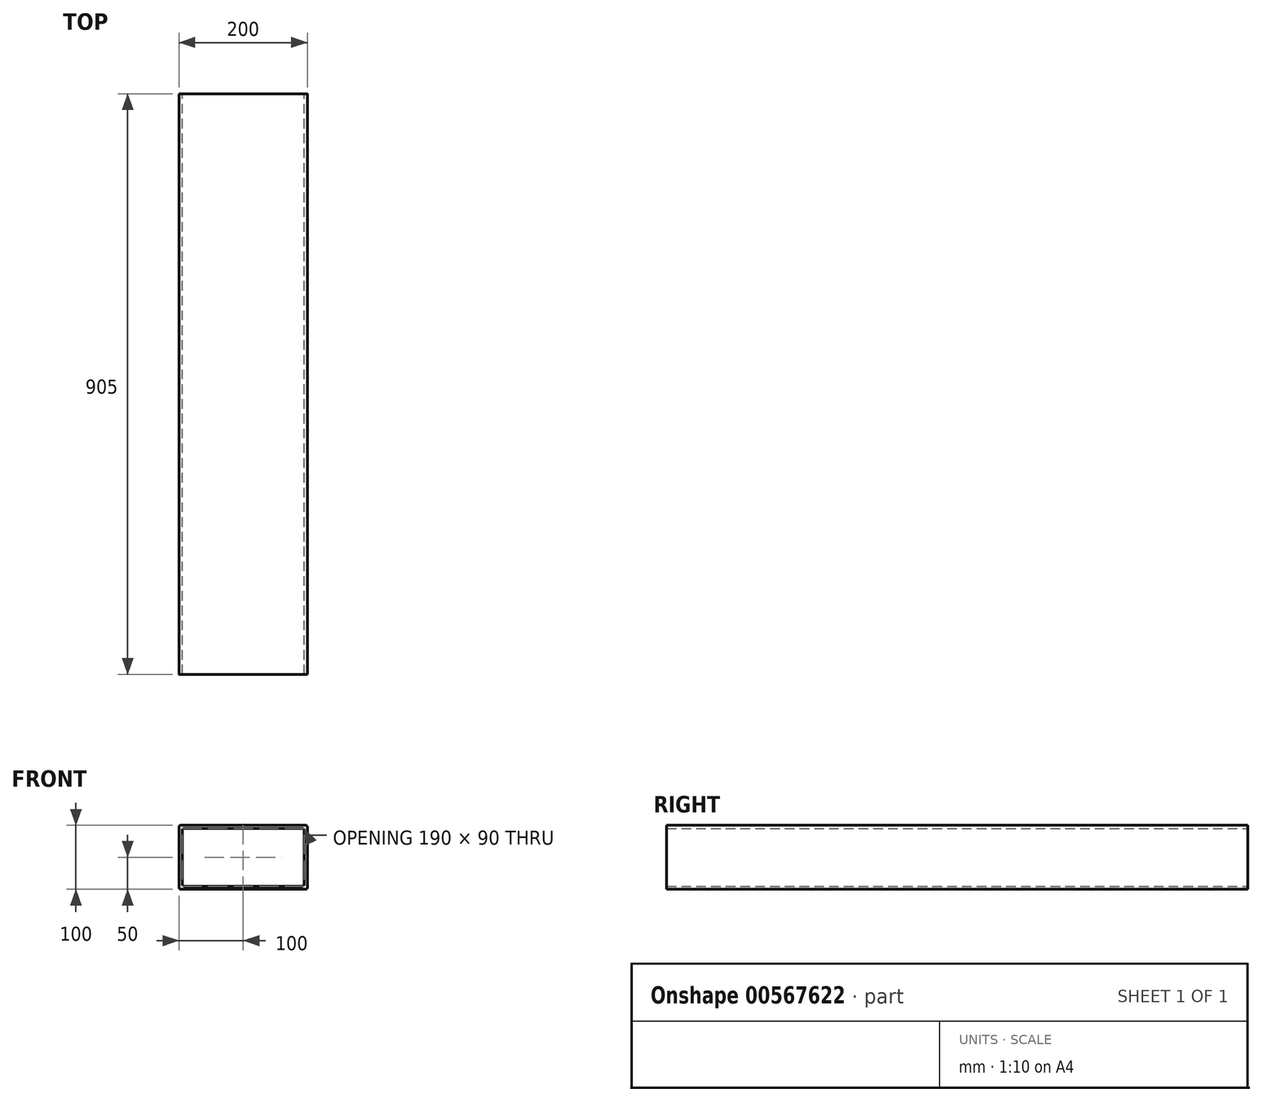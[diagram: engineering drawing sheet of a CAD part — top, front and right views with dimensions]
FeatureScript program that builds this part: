
annotation { "Feature Type Name" : "Feature", "Feature Type Description" : "" }
export const myFeature = defineFeature(function(context is Context, id is Id, definition is map)
    precondition{}
    {
        {
            var Q0;
            Q0=qCreatedBy(makeId("Front.planeOp"),FACE);
            var sketch = newSketch(context, id + "F0", { "sketchPlane" : qUnion([Q0])});
            skLineSegment(sketch, "E0.bottom", {"start": v(97, -50) * mm, "end": v(-97, -50) * mm});
            skLineSegment(sketch, "E0.top", {"start": v(97, 50) * mm, "end": v(-97, 50) * mm});
            skLineSegment(sketch, "E0.left", {"start": v(100, -47) * mm, "end": v(100, 47) * mm});
            skLineSegment(sketch, "E0.right", {"start": v(-100, -47) * mm, "end": v(-100, 47) * mm});
            skPoint(sketch, "E0.middle", {"position": v(0, 0) * mm});
            skLineSegment(sketch, "E1.bottom", {"start": v(92, -45) * mm, "end": v(-92, -45) * mm});
            skLineSegment(sketch, "E1.top", {"start": v(92, 45) * mm, "end": v(-92, 45) * mm});
            skLineSegment(sketch, "E1.left", {"start": v(95, -42) * mm, "end": v(95, 42) * mm});
            skLineSegment(sketch, "E1.right", {"start": v(-95, -42) * mm, "end": v(-95, 42) * mm});
            skPoint(sketch, "E2.visualSharp", {"position": v(-95, 45) * mm});
            skArc(sketch, "E2.filletArc", {"start": v(-92, 45) * mm, "mid": v(-94.12, 44.12) * mm, "end": v(-95, 42) * mm});
            skPoint(sketch, "E3.visualSharp", {"position": v(-100, 50) * mm});
            skArc(sketch, "E3.filletArc", {"start": v(-97, 50) * mm, "mid": v(-99.12, 49.12) * mm, "end": v(-100, 47) * mm});
            skPoint(sketch, "E4.visualSharp", {"position": v(-95, -45) * mm});
            skArc(sketch, "E4.filletArc", {"start": v(-95, -42) * mm, "mid": v(-94.12, -44.12) * mm, "end": v(-92, -45) * mm});
            skPoint(sketch, "E5.visualSharp", {"position": v(-100, -50) * mm});
            skArc(sketch, "E5.filletArc", {"start": v(-100, -47) * mm, "mid": v(-99.12, -49.12) * mm, "end": v(-97, -50) * mm});
            skPoint(sketch, "E6.visualSharp", {"position": v(95, 45) * mm});
            skArc(sketch, "E6.filletArc", {"start": v(95, 42) * mm, "mid": v(94.12, 44.12) * mm, "end": v(92, 45) * mm});
            skPoint(sketch, "E7.visualSharp", {"position": v(100, 50) * mm});
            skArc(sketch, "E7.filletArc", {"start": v(100, 47) * mm, "mid": v(99.12, 49.12) * mm, "end": v(97, 50) * mm});
            skPoint(sketch, "E8.visualSharp", {"position": v(95, -45) * mm});
            skArc(sketch, "E8.filletArc", {"start": v(92, -45) * mm, "mid": v(94.12, -44.12) * mm, "end": v(95, -42) * mm});
            skPoint(sketch, "E9.visualSharp", {"position": v(100, -50) * mm});
            skArc(sketch, "E9.filletArc", {"start": v(97, -50) * mm, "mid": v(99.12, -49.12) * mm, "end": v(100, -47) * mm});
            skSolve(sketch);
        }
        {
            var Q0;
            Q0 = qSketchRegion(id + "F0", true);
            extrude(context, id + "F1", {"entities" : qUnion([Q0]), "depth" : 905 * mm, "offsetDistance" : 25 * mm});
        }
    });
